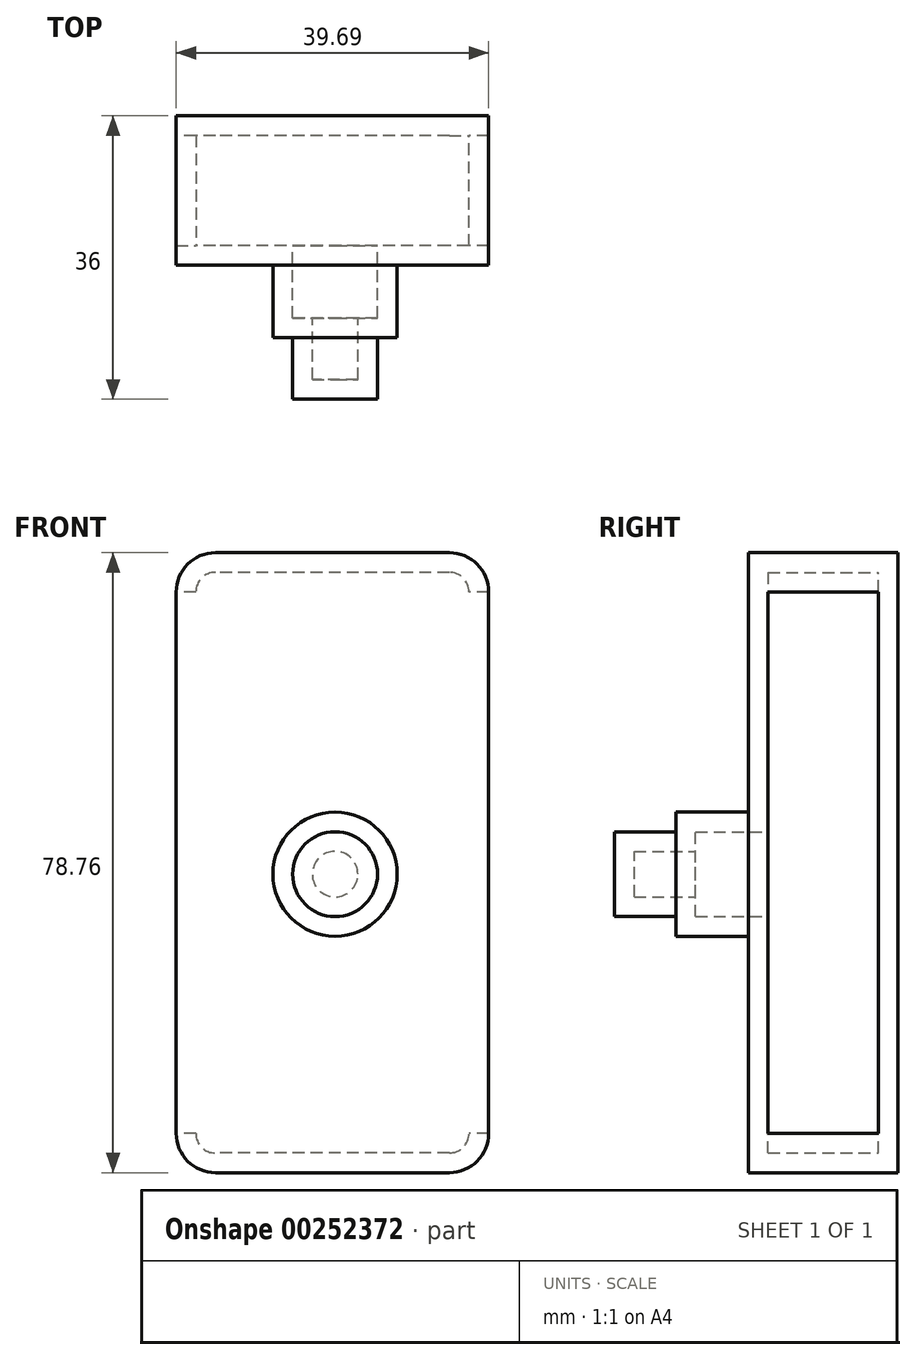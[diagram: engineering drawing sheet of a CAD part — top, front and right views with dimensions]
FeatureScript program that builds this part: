
annotation { "Feature Type Name" : "Feature", "Feature Type Description" : "" }
export const myFeature = defineFeature(function(context is Context, id is Id, definition is map)
    precondition{}
    {
        {
            var Q0;
            Q0=qCreatedBy(makeId("Front.planeOp"),FACE);
            var sketch = newSketch(context, id + "F0", { "sketchPlane" : qUnion([Q0])});
            skCircle(sketch, "E0", {"center": v(0, 0) * mm, "radius": 7.9 * mm});
            skSolve(sketch);
        }
        {
            var Q0;
            Q0=makeQuery(id+"F0.imprint","IMPRINT",FACE,{"disambiguationData":[TD([[makeQuery(id+"F0.imprint","IMPRINT",EDGE,{"derivedFrom":sQuery(id+"F0.wireOp",EDGE,"E0")}),1.0]])]});
            extrude(context, id + "F1", {"entities" : qUnion([Q0]), "depth" : 9.2 * mm});
        }
        {
            var Q0;
            Q0=makeQuery(id+"F1.opExtrude","CAP_FACE",FACE,{"disambiguationData":[OSD([sQuery(id+"F0.wireOp",EDGE,"E0")])],"isStart":false});
            shell(context, id + "F2", {"entities" : qUnion([Q0]), "thickness" : 2.5 * mm});
        }
        {
            var Q0;
            {var subQ0=sQuery(id+"F0.wireOp",EDGE,"E0");Q0=makeQuery(id+"F2.opShell","OFFSET_FACE",FACE,{"disambiguationData":[OSD([subQ0]),TDD([makeQuery(id+"F1.opExtrude","CAP_FACE",FACE,{"disambiguationData":[OSD([subQ0])],"isStart":true})])]});}
            extrude(context, id + "F3", {"entities" : qUnion([Q0]), "operationType" : NewBodyOperationType.ADD, "depth" : 14.5 * mm});
        }
        {
            var Q0;
            Q0=qCreatedBy(makeId("Front.planeOp"),FACE);
            var sketch = newSketch(context, id + "F4", { "sketchPlane" : qUnion([Q0])});
            skLineSegment(sketch, "E1.bottom", {"start": v(19.5, 40.84) * mm, "end": v(-20.18, 40.84) * mm});
            skLineSegment(sketch, "E1.top", {"start": v(19.5, -37.92) * mm, "end": v(-20.18, -37.92) * mm});
            skLineSegment(sketch, "E1.left", {"start": v(19.5, 40.84) * mm, "end": v(19.5, -37.92) * mm});
            skLineSegment(sketch, "E1.right", {"start": v(-20.18, 40.84) * mm, "end": v(-20.18, -37.92) * mm});
            skSolve(sketch);
        }
        {
            var Q0;
            Q0=makeQuery(id+"F4.imprint","IMPRINT",FACE,{"disambiguationData":[TD([[makeQuery(id+"F4.imprint","IMPRINT",EDGE,{"derivedFrom":sQuery(id+"F4.wireOp",EDGE,"E1.bottom")}),1.0]])]});
            extrude(context, id + "F5", {"entities" : qUnion([Q0]), "operationType" : NewBodyOperationType.ADD, "oppositeDirection" : true, "depth" : 19 * mm});
        }
        {
            var Q0;
            Q0=makeQuery(id+"F5.opExtrude","SWEPT_EDGE",EDGE,{"disambiguationData":[OSD([sQuery(id+"F4.wireOp",EDGE,"E1.bottom"),sQuery(id+"F4.wireOp",EDGE,"E1.left")])]});
            var Q1;
            Q1=makeQuery(id+"F5.opExtrude","SWEPT_EDGE",EDGE,{"disambiguationData":[OSD([sQuery(id+"F4.wireOp",EDGE,"E1.top"),sQuery(id+"F4.wireOp",EDGE,"E1.left")])]});
            var Q2;
            Q2=makeQuery(id+"F5.opExtrude","SWEPT_EDGE",EDGE,{"disambiguationData":[OSD([sQuery(id+"F4.wireOp",EDGE,"E1.bottom"),sQuery(id+"F4.wireOp",EDGE,"E1.right")])]});
            var Q3;
            Q3=makeQuery(id+"F5.opExtrude","SWEPT_EDGE",EDGE,{"disambiguationData":[OSD([sQuery(id+"F4.wireOp",EDGE,"E1.top"),sQuery(id+"F4.wireOp",EDGE,"E1.right")])]});
            fillet(context, id + "F6", {"entities" : qUnion([Q0, Q1, Q2, Q3]), "radius" : 5 * mm, "tangentPropagation" : true, "allowEdgeOverflow" : false});
        }
        {
            var Q0;
            Q0=makeQuery(id+"F5.opExtrude","SWEPT_FACE",FACE,{"disambiguationData":[OSD([sQuery(id+"F4.wireOp",EDGE,"E1.left")])]});
            var Q1;
            Q1=makeQuery(id+"F5.opExtrude","SWEPT_FACE",FACE,{"disambiguationData":[OSD([sQuery(id+"F4.wireOp",EDGE,"E1.right")])]});
            shell(context, id + "F7", {"entities" : qUnion([Q0, Q1]), "thickness" : 2.5 * mm});
        }
    });
